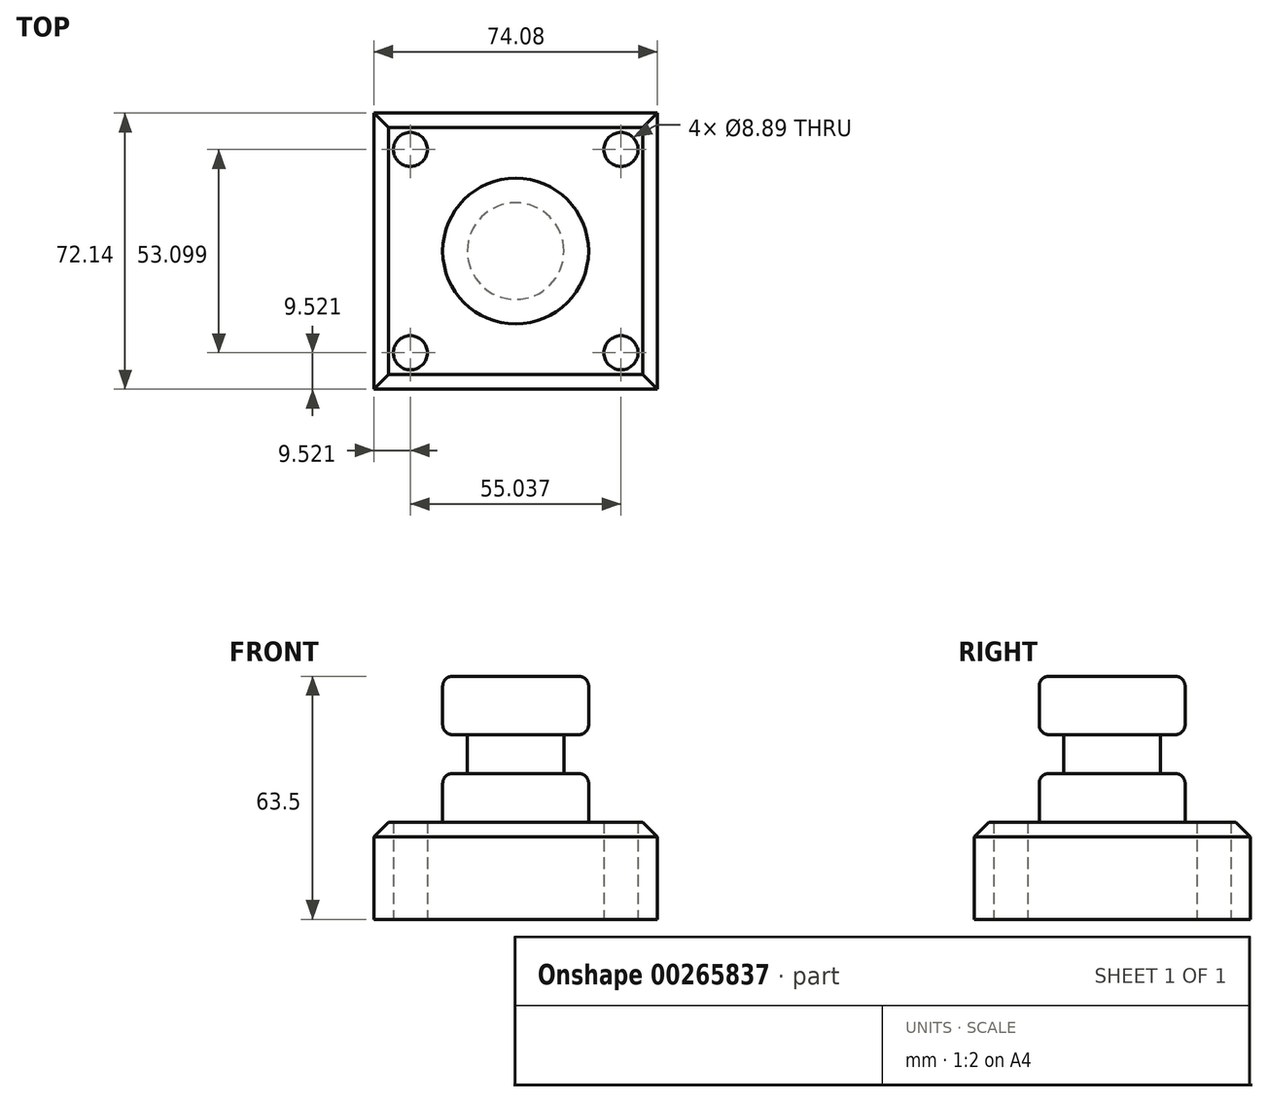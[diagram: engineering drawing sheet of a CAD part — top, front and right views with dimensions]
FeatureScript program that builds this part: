
annotation { "Feature Type Name" : "Feature", "Feature Type Description" : "" }
export const myFeature = defineFeature(function(context is Context, id is Id, definition is map)
    precondition{}
    {
        {
            var Q0;
            Q0=qCreatedBy(makeId("Top.planeOp"),FACE);
            var sketch = newSketch(context, id + "F0", { "sketchPlane" : qUnion([Q0])});
            skLineSegment(sketch, "E0.bottom", {"start": v(-37.04, 36.07) * mm, "end": v(37.04, 36.07) * mm});
            skLineSegment(sketch, "E0.top", {"start": v(-37.04, -36.07) * mm, "end": v(37.04, -36.07) * mm});
            skLineSegment(sketch, "E0.left", {"start": v(-37.04, 36.07) * mm, "end": v(-37.04, -36.07) * mm});
            skLineSegment(sketch, "E0.right", {"start": v(37.04, 36.07) * mm, "end": v(37.04, -36.07) * mm});
            skPoint(sketch, "E0.middle", {"position": v(0, 0) * mm});
            skSolve(sketch);
        }
        {
            var Q0;
            Q0 = qSketchRegion(id + "F0", true);
            extrude(context, id + "F1", {"entities" : qUnion([Q0]), "depth" : 25.4 * mm});
        }
        {
            var Q0;
            Q0=makeQuery(id+"F1.opExtrude","CAP_FACE",FACE,{"disambiguationData":[OSD([sQuery(id+"F0.wireOp",EDGE,"E0.bottom"),sQuery(id+"F0.wireOp",EDGE,"E0.top"),sQuery(id+"F0.wireOp",EDGE,"E0.left"),sQuery(id+"F0.wireOp",EDGE,"E0.right")])],"isStart":true});
            var sketch = newSketch(context, id + "F2", { "sketchPlane" : qUnion([Q0])});
            skCircle(sketch, "E1", {"center": v(27.52, -26.55) * mm, "radius": 4.45 * mm});
            skCircle(sketch, "E2", {"center": v(27.52, 26.55) * mm, "radius": 4.45 * mm});
            skCircle(sketch, "E3", {"center": v(-27.52, 26.55) * mm, "radius": 4.45 * mm});
            skCircle(sketch, "E4", {"center": v(-27.52, -26.55) * mm, "radius": 4.45 * mm});
            skSolve(sketch);
        }
        {
            var Q0;
            Q0 = qSketchRegion(id + "F2", true);
            extrude(context, id + "F3", {"entities" : qUnion([Q0]), "operationType" : NewBodyOperationType.REMOVE, "oppositeDirection" : true, "depth" : 25.4 * mm});
        }
        {
            var Q0;
            Q0=qCreatedBy(makeId("Front.planeOp"),FACE);
            var sketch = newSketch(context, id + "F4", { "sketchPlane" : qUnion([Q0])});
            skLineSegment(sketch, "E5.bottom", {"start": v(-19.05, 63.5) * mm, "end": v(0, 63.5) * mm});
            skLineSegment(sketch, "E5.top", {"start": v(-19.05, 25.4) * mm, "end": v(0, 25.4) * mm});
            skLineSegment(sketch, "E5.left", {"start": v(-19.05, 63.5) * mm, "end": v(-19.05, 25.4) * mm});
            skLineSegment(sketch, "E5.right", {"start": v(0, 63.5) * mm, "end": v(0, 25.4) * mm});
            skPoint(sketch, "E6.firstSnap0", {"position": v(-19.05, 44.45) * mm});
            skSolve(sketch);
        }
        {
            var Q0;
            Q0=makeQuery(id+"F4.imprint","IMPRINT",FACE,{"disambiguationData":[TD([[makeQuery(id+"F4.imprint","IMPRINT",EDGE,{"derivedFrom":sQuery(id+"F4.wireOp",EDGE,"E5.bottom")}),-1.0]])]});
            var Q1;
            Q1=sQuery(id+"F4.wireOp",EDGE,"E5.right");
            revolve(context, id + "F5", {"operationType" : NewBodyOperationType.ADD, "entities" : qUnion([Q0]), "axis" : qUnion([Q1]), "revolveType" : RevolveType.FULL});
        }
        {
            var Q0;
            Q0=qCreatedBy(makeId("Right.planeOp"),FACE);
            var sketch = newSketch(context, id + "F6", { "sketchPlane" : qUnion([Q0])});
            skLineSegment(sketch, "E7.bottom", {"start": v(23.04, 48.26) * mm, "end": v(12.6, 48.26) * mm});
            skLineSegment(sketch, "E7.top", {"start": v(23.04, 38.1) * mm, "end": v(12.6, 38.1) * mm});
            skLineSegment(sketch, "E7.left", {"start": v(23.04, 48.26) * mm, "end": v(23.04, 38.1) * mm});
            skLineSegment(sketch, "E7.right", {"start": v(12.6, 48.26) * mm, "end": v(12.6, 38.1) * mm});
            skSolve(sketch);
        }
        {
            var Q0;
            Q0 = qSketchRegion(id + "F6", true);
            var Q1;
            Q1=makeQuery(id+"F5.opRevolve","SWEPT_FACE",FACE,{"disambiguationData":[OSD([sQuery(id+"F4.wireOp",EDGE,"E5.left")])]});
            revolve(context, id + "F7", {"operationType" : NewBodyOperationType.REMOVE, "entities" : qUnion([Q0]), "axis" : qUnion([Q1]), "revolveType" : RevolveType.FULL, "oppositeDirection" : true});
        }
        {
            var Q0;
            Q0=makeQuery(id+"F1.opExtrude","CAP_EDGE",EDGE,{"disambiguationData":[OSD([sQuery(id+"F0.wireOp",EDGE,"E0.left")])],"isStart":false});
            var Q1;
            Q1=makeQuery(id+"F1.opExtrude","CAP_EDGE",EDGE,{"disambiguationData":[OSD([sQuery(id+"F0.wireOp",EDGE,"E0.top")])],"isStart":false});
            var Q2;
            Q2=makeQuery(id+"F1.opExtrude","CAP_EDGE",EDGE,{"disambiguationData":[OSD([sQuery(id+"F0.wireOp",EDGE,"E0.right")])],"isStart":false});
            var Q3;
            Q3=makeQuery(id+"F1.opExtrude","CAP_EDGE",EDGE,{"disambiguationData":[OSD([sQuery(id+"F0.wireOp",EDGE,"E0.bottom")])],"isStart":false});
            chamfer(context, id + "F8", {"entities" : qUnion([Q0, Q1, Q2, Q3]), "width" : 3.8 * mm, "tangentPropagation" : true});
        }
        {
            var Q0;
            Q0=makeQuery(id+"F7.boolean.opBoolean","INTERSECT",EDGE,{"derivedFrom":[makeQuery(id+"F5.opRevolve","SWEPT_FACE",FACE,{"disambiguationData":[OSD([sQuery(id+"F4.wireOp",EDGE,"E5.left")])]}),makeQuery(id+"F7.opRevolve","SWEPT_FACE",FACE,{"disambiguationData":[OSD([sQuery(id+"F6.wireOp",EDGE,"E7.top")])]})]});
            var Q1;
            Q1=makeQuery(id+"F7.boolean.opBoolean","INTERSECT",EDGE,{"derivedFrom":[makeQuery(id+"F5.opRevolve","SWEPT_FACE",FACE,{"disambiguationData":[OSD([sQuery(id+"F4.wireOp",EDGE,"E5.left")])]}),makeQuery(id+"F7.opRevolve","SWEPT_FACE",FACE,{"disambiguationData":[OSD([sQuery(id+"F6.wireOp",EDGE,"E7.bottom")])]})]});
            var Q2;
            Q2=makeQuery(id+"F5.opRevolve","SWEPT_EDGE",EDGE,{"disambiguationData":[OSD([sQuery(id+"F4.wireOp",EDGE,"E5.top"),sQuery(id+"F4.wireOp",EDGE,"E5.left")])]});
            fillet(context, id + "F9", {"entities" : qUnion([Q0, Q1, Q2]), "radius" : 2.54 * mm, "tangentPropagation" : true, "allowEdgeOverflow" : false});
        }
        {
            var Q0;
            Q0=makeQuery(id+"F5.opRevolve","SWEPT_EDGE",EDGE,{"disambiguationData":[OSD([sQuery(id+"F4.wireOp",EDGE,"E5.bottom"),sQuery(id+"F4.wireOp",EDGE,"E5.left")])]});
            fillet(context, id + "F10", {"entities" : qUnion([Q0]), "radius" : 2.54 * mm, "tangentPropagation" : true, "allowEdgeOverflow" : false});
        }
    });
